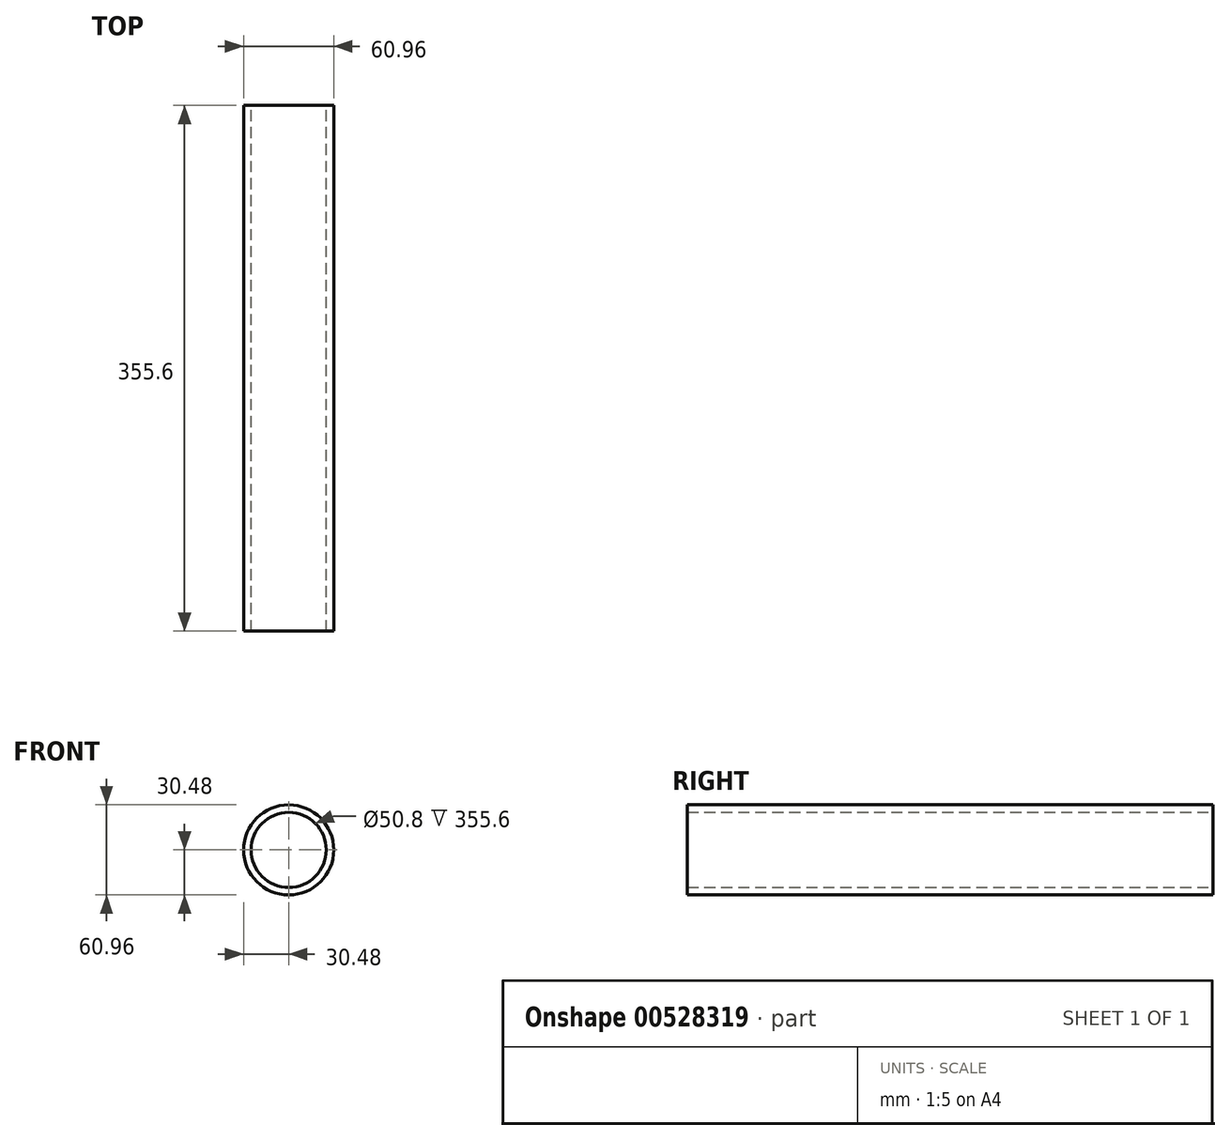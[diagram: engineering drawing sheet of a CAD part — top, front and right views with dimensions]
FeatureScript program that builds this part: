
annotation { "Feature Type Name" : "Feature", "Feature Type Description" : "" }
export const myFeature = defineFeature(function(context is Context, id is Id, definition is map)
    precondition{}
    {
        {
            var Q0;
            Q0=qCreatedBy(makeId("Front.planeOp"),FACE);
            var sketch = newSketch(context, id + "F0", { "sketchPlane" : qUnion([Q0])});
            skCircle(sketch, "E0", {"center": v(0, 0) * mm, "radius": 30.48 * mm});
            skCircle(sketch, "E1", {"center": v(0, 0) * mm, "radius": 25.4 * mm});
            skSolve(sketch);
        }
        {
            var Q0;
            Q0=makeQuery(id+"F0.imprint","IMPRINT",FACE,{"disambiguationData":[TD([[makeQuery(id+"F0.imprint","IMPRINT",EDGE,{"derivedFrom":sQuery(id+"F0.wireOp",EDGE,"E0")}),1.0]])]});
            extrude(context, id + "F1", {"entities" : qUnion([Q0]), "depth" : 228.6 * mm, "offsetDistance" : 25.4 * mm, "hasSecondDirection" : true, "secondDirectionOppositeDirection" : true, "secondDirectionDepth" : 127 * mm});
        }
    });
